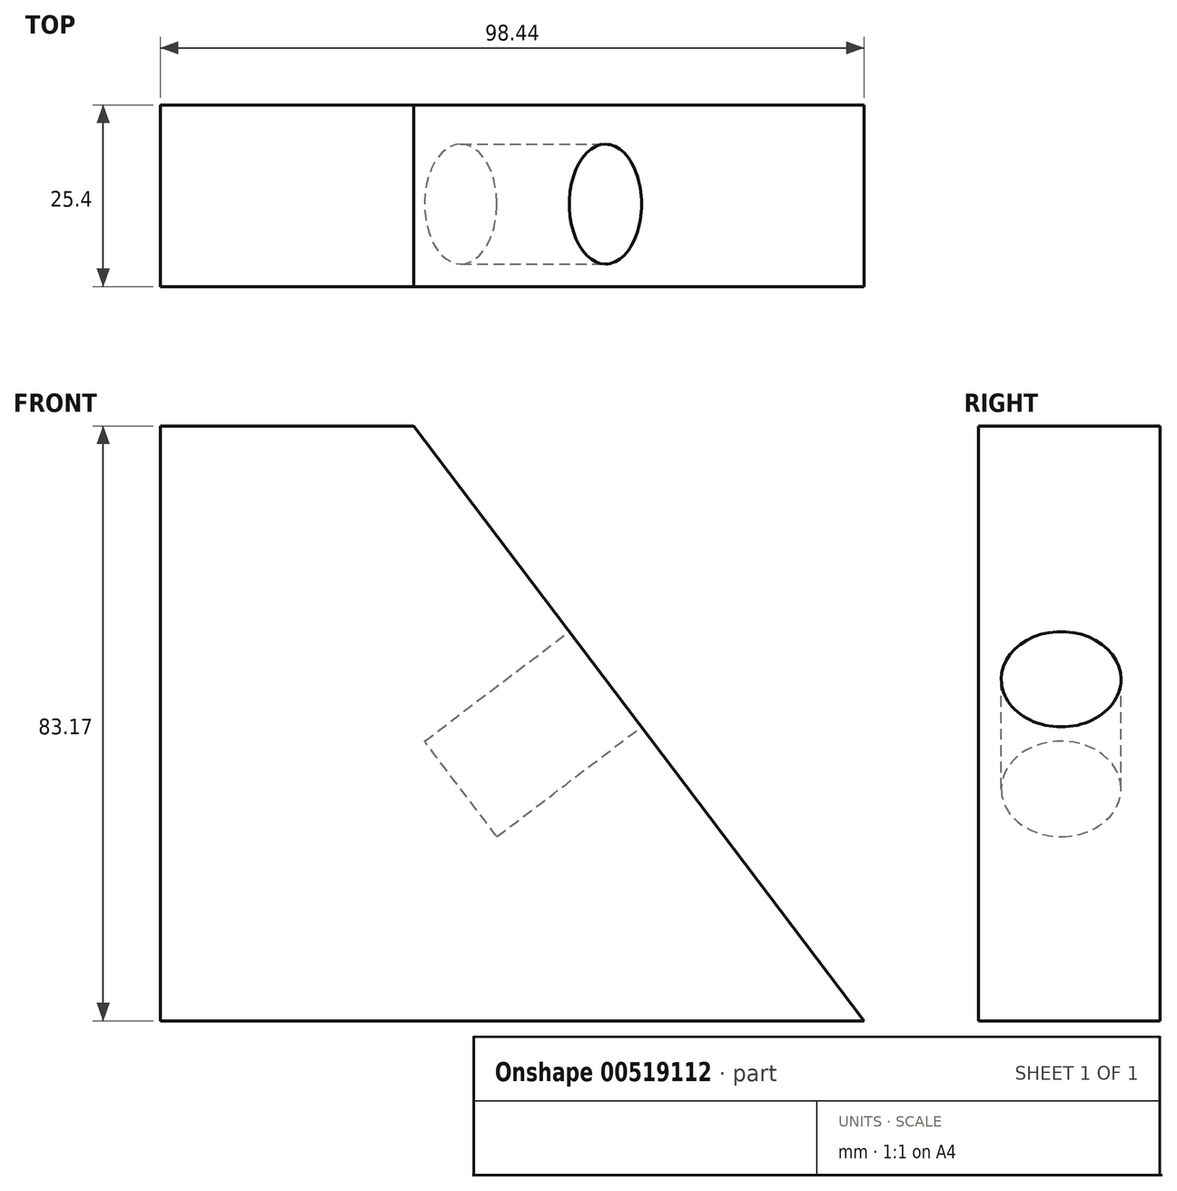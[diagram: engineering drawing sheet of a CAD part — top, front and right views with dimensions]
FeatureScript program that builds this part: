
annotation { "Feature Type Name" : "Feature", "Feature Type Description" : "" }
export const myFeature = defineFeature(function(context is Context, id is Id, definition is map)
    precondition{}
    {
        {
            var Q0;
            Q0=qCreatedBy(makeId("Front.planeOp"),FACE);
            var sketch = newSketch(context, id + "F0", { "sketchPlane" : qUnion([Q0])});
            skLineSegment(sketch, "E0", {"start": v(-49.38, 51.17) * mm, "end": v(-49.38, -32) * mm});
            skLineSegment(sketch, "E1", {"start": v(-49.38, -32) * mm, "end": v(49.06, -32) * mm});
            skLineSegment(sketch, "E2", {"start": v(-49.38, 51.17) * mm, "end": v(-13.97, 51.17) * mm});
            skLineSegment(sketch, "E3", {"start": v(-13.97, 51.17) * mm, "end": v(49.06, -32) * mm});
            skSolve(sketch);
        }
        {
            var Q0;
            Q0 = qSketchRegion(id + "F0", true);
            extrude(context, id + "F1", {"entities" : qUnion([Q0]), "depth" : 25.4 * mm});
        }
        {
            var Q0;
            Q0=makeQuery(id+"F1.opExtrude","SWEPT_FACE",FACE,{"disambiguationData":[OSD([sQuery(id+"F0.wireOp",EDGE,"E3")])]});
            var sketch = newSketch(context, id + "F2", { "sketchPlane" : qUnion([Q0])});
            skCircle(sketch, "E4", {"center": v(-13.86, 4.8) * mm, "radius": 8.37 * mm});
            skSolve(sketch);
        }
        {
            var Q0;
            Q0 = qSketchRegion(id + "F2", true);
            extrude(context, id + "F3", {"entities" : qUnion([Q0]), "operationType" : NewBodyOperationType.REMOVE, "oppositeDirection" : true, "depth" : 25.4 * mm, "hasSecondDirection" : true, "secondDirectionOppositeDirection" : false, "secondDirectionDepth" : 25.4 * mm});
        }
    });
